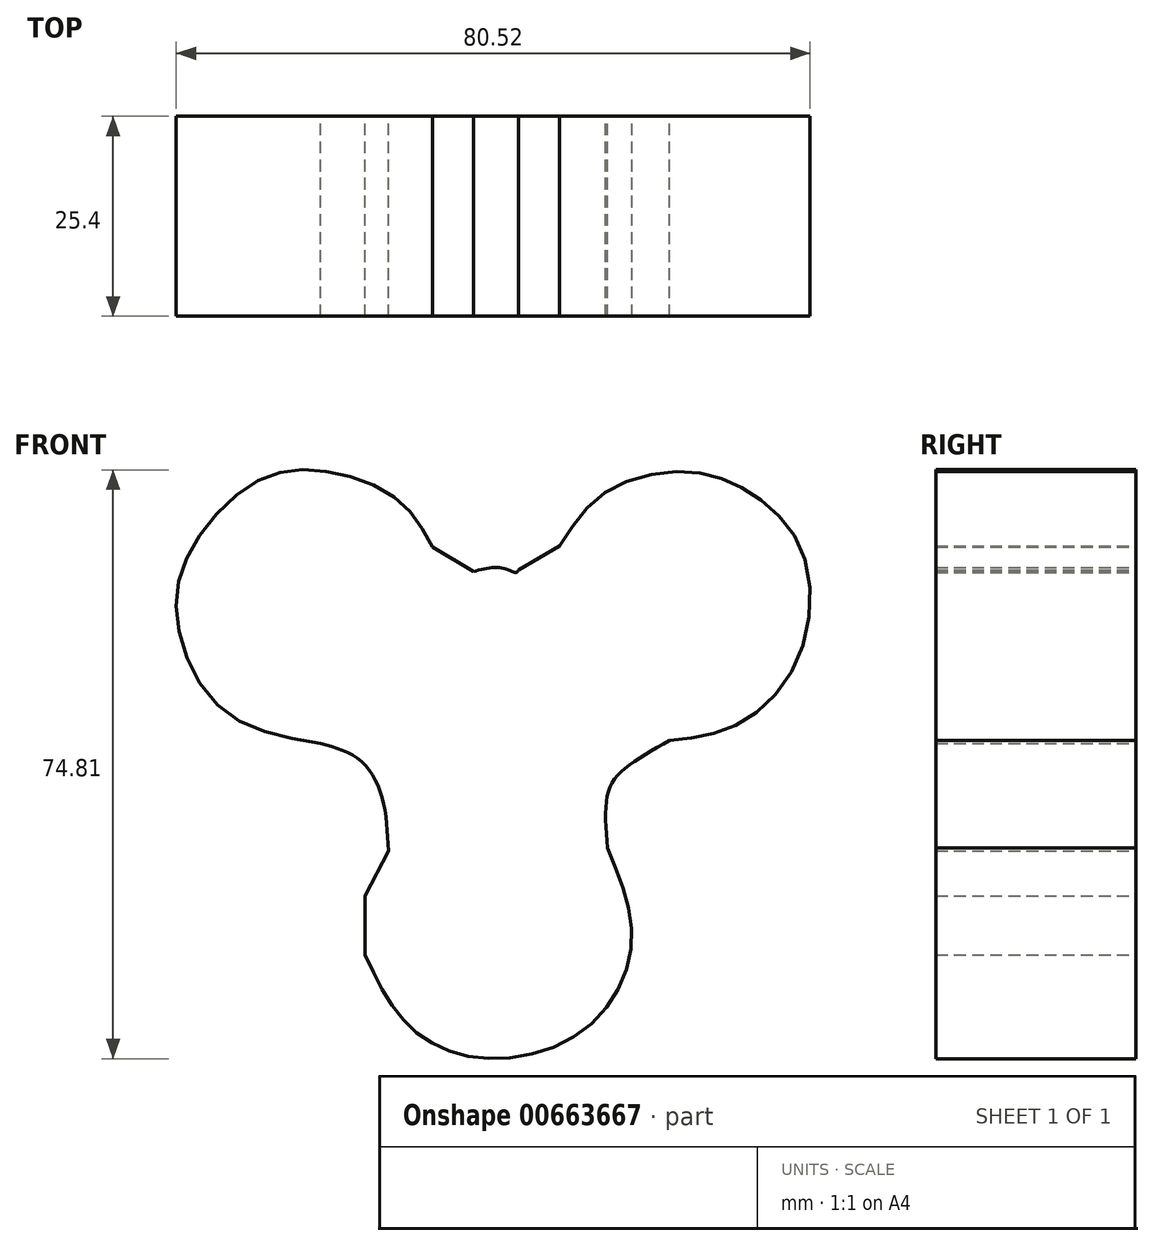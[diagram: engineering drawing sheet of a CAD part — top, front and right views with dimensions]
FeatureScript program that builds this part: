
annotation { "Feature Type Name" : "Feature", "Feature Type Description" : "" }
export const myFeature = defineFeature(function(context is Context, id is Id, definition is map)
    precondition{}
    {
        {
            var Q0;
            Q0=qCreatedBy(makeId("Front.planeOp"),FACE);
            var sketch = newSketch(context, id + "F0", { "sketchPlane" : qUnion([Q0])});
            skFitSpline(sketch, "E0", {"points": [v(-27.63, -20.39) * mm, v(-22.25, -29.16) * mm, v(-13.12, -33.46) * mm, v(0, -30.06) * mm, v(6.23, -18.95) * mm, v(3.18, -6.77) * mm], "startDerivative": vector(24.4, -51.4) * mm, "endDerivative": vector(-24.36, 58.56) * mm});
            skFitSpline(sketch, "E1", {"points": [v(3.18, -6.77) * mm, v(3.18, 0) * mm, v(5.15, 3.08) * mm, v(11.07, 6.84) * mm], "startDerivative": vector(-1.68, 20.69) * mm, "endDerivative": vector(18.14, 10.22) * mm});
            skFitSpline(sketch, "E2", {"points": [v(11.07, 6.84) * mm, v(19.49, 8.81) * mm, v(27.37, 17.23) * mm, v(27.9, 30.85) * mm, v(21.28, 38.37) * mm, v(13.4, 41.01) * mm, v(3.18, 38.55) * mm, v(-2.9, 31.57) * mm], "startDerivative": vector(64.79, 7.06) * mm, "endDerivative": vector(-37.43, -57.99) * mm});
            skFitSpline(sketch, "E3", {"points": [v(-2.9, 31.57) * mm, v(-8.1, 28.52) * mm], "startDerivative": vector(-5.2, -3.05) * mm, "endDerivative": vector(-5.2, -3.05) * mm});
            skFitSpline(sketch, "E4", {"points": [v(-8.1, 28.52) * mm, v(-8.4, 28.22) * mm, v(-10.18, 28.8) * mm, v(-13.86, 28.3) * mm], "startDerivative": vector(-1.34, -2.53) * mm, "endDerivative": vector(-7.94, -2.19) * mm});
            skFitSpline(sketch, "E5", {"points": [v(-13.86, 28.3) * mm, v(-19.05, 31.47) * mm], "startDerivative": vector(-5.19, 3.16) * mm, "endDerivative": vector(-5.19, 3.16) * mm});
            skFitSpline(sketch, "E6", {"points": [v(-19.05, 31.47) * mm, v(-23.44, 37.42) * mm, v(-32.45, 41.01) * mm, v(-41.1, 39.9) * mm, v(-49.53, 31.47) * mm, v(-51.42, 21.64) * mm, v(-45.5, 10.62) * mm, v(-33.28, 6.46) * mm], "startDerivative": vector(-29.2, 53.56) * mm, "endDerivative": vector(84.02, -14.13) * mm});
            skFitSpline(sketch, "E7", {"points": [v(-33.28, 6.46) * mm, v(-28.54, 4.57) * mm, v(-25.57, 0) * mm, v(-24.62, -7.17) * mm], "startDerivative": vector(16.46, -4.3) * mm, "endDerivative": vector(1.1, -20.3) * mm});
            skFitSpline(sketch, "E8", {"points": [v(-27.63, -20.39) * mm, v(-27.63, -12.85) * mm], "startDerivative": vector(0, 7.53) * mm, "endDerivative": vector(0, 7.53) * mm});
            skFitSpline(sketch, "E9", {"points": [v(-27.63, -12.85) * mm, v(-24.62, -7.17) * mm], "startDerivative": vector(3, 5.68) * mm, "endDerivative": vector(3, 5.68) * mm});
            skSolve(sketch);
        }
        {
            var Q0;
            Q0=makeQuery(id+"F0.imprint","IMPRINT",FACE,{"disambiguationData":[TD([[makeQuery(id+"F0.imprint","IMPRINT",EDGE,{"derivedFrom":sQuery(id+"F0.wireOp",EDGE,"E0")}),1.0]])]});
            extrude(context, id + "F1", {"entities" : qUnion([Q0]), "depth" : 25.4 * mm, "offsetDistance" : 25.4 * mm});
        }
    });
